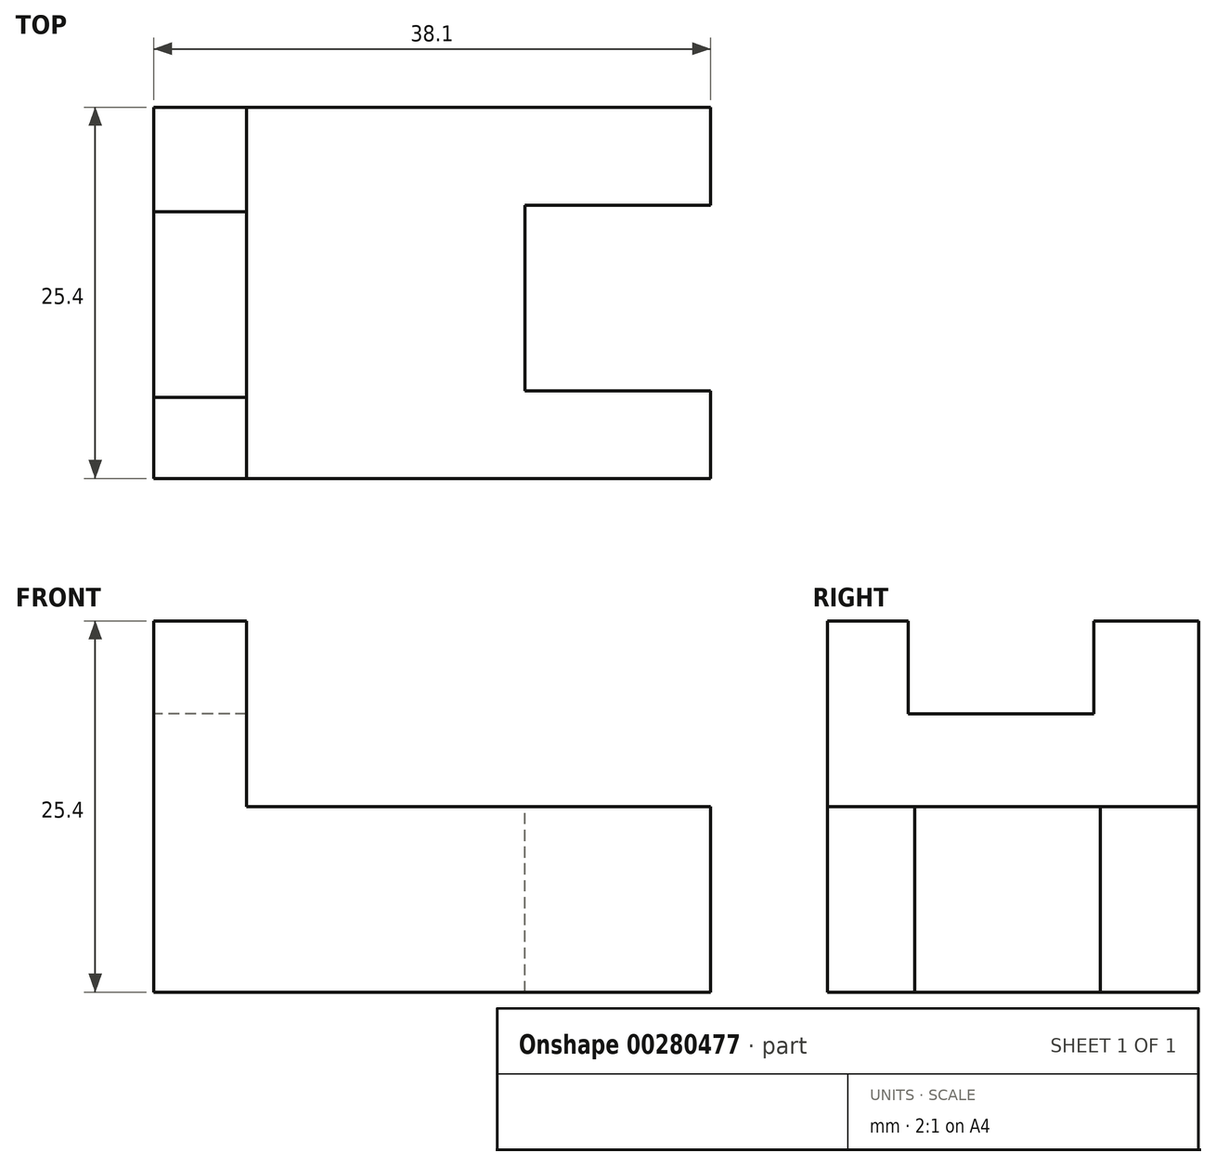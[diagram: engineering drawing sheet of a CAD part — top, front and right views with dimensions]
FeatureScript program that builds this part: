
annotation { "Feature Type Name" : "Feature", "Feature Type Description" : "" }
export const myFeature = defineFeature(function(context is Context, id is Id, definition is map)
    precondition{}
    {
        {
            var Q0;
            Q0=qCreatedBy(makeId("Front.planeOp"),FACE);
            var sketch = newSketch(context, id + "F0", { "sketchPlane" : qUnion([Q0])});
            skLineSegment(sketch, "E0", {"start": v(0, 0) * mm, "end": v(0, 25.4) * mm});
            skLineSegment(sketch, "E1", {"start": v(0, 25.4) * mm, "end": v(6.35, 25.4) * mm});
            skLineSegment(sketch, "E2", {"start": v(6.35, 25.4) * mm, "end": v(6.35, 12.7) * mm});
            skLineSegment(sketch, "E3", {"start": v(0, 0) * mm, "end": v(38.1, 0) * mm});
            skLineSegment(sketch, "E4", {"start": v(38.1, 0) * mm, "end": v(38.1, 12.7) * mm});
            skLineSegment(sketch, "E5", {"start": v(38.1, 12.7) * mm, "end": v(6.35, 12.7) * mm});
            skSolve(sketch);
        }
        {
            var Q0;
            Q0 = qSketchRegion(id + "F0", true);
            extrude(context, id + "F1", {"entities" : qUnion([Q0]), "depth" : 25.4 * mm});
        }
        {
            var Q0;
            Q0=qCreatedBy(makeId("Right.planeOp"),FACE);
            var sketch = newSketch(context, id + "F2", { "sketchPlane" : qUnion([Q0])});
            skLineSegment(sketch, "E6", {"start": v(-19.87, 25.4) * mm, "end": v(-19.87, 19.05) * mm});
            skLineSegment(sketch, "E7", {"start": v(-19.87, 19.05) * mm, "end": v(-7.17, 19.05) * mm});
            skLineSegment(sketch, "E8", {"start": v(-7.17, 19.05) * mm, "end": v(-7.17, 25.4) * mm});
            skLineSegment(sketch, "E9", {"start": v(-7.17, 25.4) * mm, "end": v(-19.87, 25.4) * mm});
            skSolve(sketch);
        }
        {
            var Q0;
            Q0 = qSketchRegion(id + "F2", true);
            extrude(context, id + "F3", {"entities" : qUnion([Q0]), "operationType" : NewBodyOperationType.REMOVE, "depth" : 35.05 * mm});
        }
        {
            var Q0;
            Q0=makeQuery(id+"F1.opExtrude","SWEPT_FACE",FACE,{"disambiguationData":[OSD([sQuery(id+"F0.wireOp",EDGE,"E5")])]});
            var sketch = newSketch(context, id + "F4", { "sketchPlane" : qUnion([Q0])});
            skLineSegment(sketch, "E10", {"start": v(38.1, -6.73) * mm, "end": v(25.4, -6.73) * mm});
            skLineSegment(sketch, "E11", {"start": v(25.4, -6.73) * mm, "end": v(25.4, -19.43) * mm});
            skLineSegment(sketch, "E12", {"start": v(25.4, -19.43) * mm, "end": v(38.1, -19.43) * mm});
            skLineSegment(sketch, "E13", {"start": v(38.1, -19.43) * mm, "end": v(38.1, -6.73) * mm});
            skSolve(sketch);
        }
        {
            var Q0;
            Q0 = qSketchRegion(id + "F4", true);
            extrude(context, id + "F5", {"entities" : qUnion([Q0]), "operationType" : NewBodyOperationType.REMOVE, "oppositeDirection" : true, "depth" : 30.48 * mm});
        }
    });
